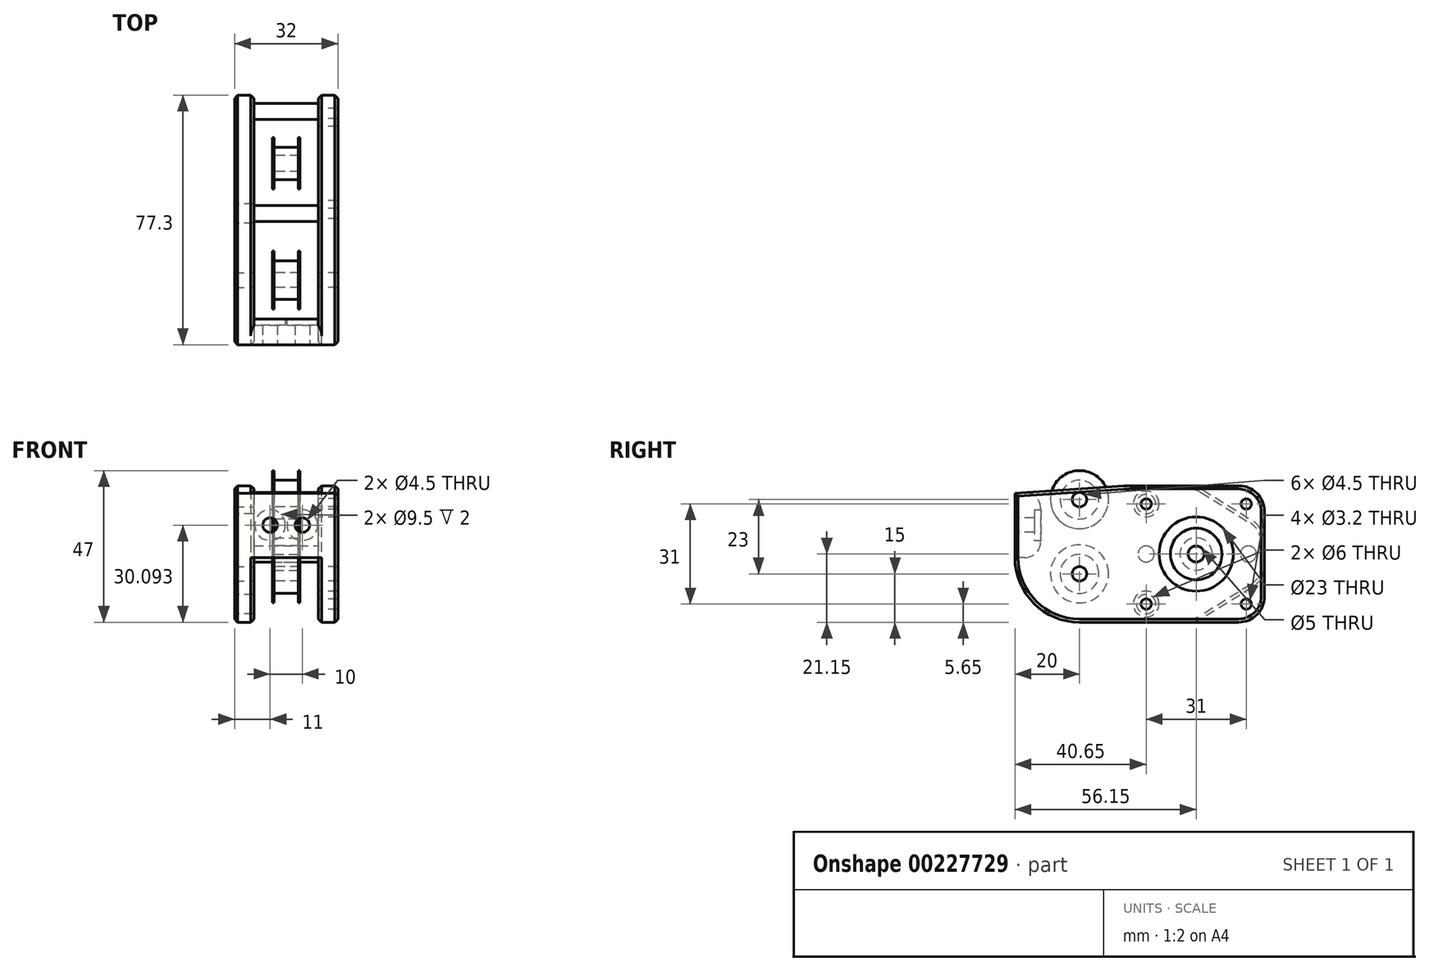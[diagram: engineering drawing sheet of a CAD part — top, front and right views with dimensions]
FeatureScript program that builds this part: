
annotation { "Feature Type Name" : "Feature", "Feature Type Description" : "" }
export const myFeature = defineFeature(function(context is Context, id is Id, definition is map)
    precondition{}
    {
        {
            var Q0;
            Q0=qCreatedBy(makeId("Right.planeOp"),FACE);
            var sketch = newSketch(context, id + "F0", { "sketchPlane" : qUnion([Q0])});
            skLineSegment(sketch, "E0.bottom", {"start": v(0, 0) * mm, "end": v(-20, 0) * mm, "construction": true});
            skLineSegment(sketch, "E0.top", {"start": v(0, 20) * mm, "end": v(-20, 20) * mm, "construction": true});
            skLineSegment(sketch, "E0.left", {"start": v(0, 0) * mm, "end": v(0, 20) * mm, "construction": true});
            skLineSegment(sketch, "E0.right", {"start": v(-20, 0) * mm, "end": v(-20, 20) * mm, "construction": true});
            skCircle(sketch, "E1", {"center": v(20, -5) * mm, "radius": 2.25 * mm});
            skCircle(sketch, "E2", {"center": v(20, -5) * mm, "radius": 9 * mm});
            skCircle(sketch, "E3", {"center": v(20, -5) * mm, "radius": 6 * mm});
            skLineSegment(sketch, "E4", {"start": v(0, 0) * mm, "end": v(0, -20) * mm, "construction": true});
            skLineSegment(sketch, "E5.bottom", {"start": v(77.3, -20) * mm, "end": v(35, -20) * mm, "construction": true});
            skLineSegment(sketch, "E5.top", {"start": v(77.3, 22.3) * mm, "end": v(35, 22.3) * mm, "construction": true});
            skLineSegment(sketch, "E5.left", {"start": v(77.3, -20) * mm, "end": v(77.3, 22.3) * mm, "construction": true});
            skLineSegment(sketch, "E5.right", {"start": v(35, -20) * mm, "end": v(35, 22.3) * mm, "construction": true});
            skLineSegment(sketch, "E6", {"start": v(35, 22.3) * mm, "end": v(77.3, -20) * mm, "construction": true});
            skCircle(sketch, "E7", {"center": v(56.15, 1.15) * mm, "radius": 2.5 * mm});
            skCircle(sketch, "E8", {"center": v(56.15, 1.15) * mm, "radius": 8 * mm});
            skCircle(sketch, "E9", {"center": v(56.15, 1.15) * mm, "radius": 5 * mm});
            skLineSegment(sketch, "E10", {"start": v(35, -20) * mm, "end": v(77.3, 22.3) * mm, "construction": true});
            skCircle(sketch, "E11", {"center": v(40.65, 16.65) * mm, "radius": 1.6 * mm, "construction": true});
            skCircle(sketch, "E12", {"center": v(71.65, 16.65) * mm, "radius": 1.6 * mm, "construction": true});
            skCircle(sketch, "E13", {"center": v(71.65, -14.35) * mm, "radius": 1.6 * mm, "construction": true});
            skCircle(sketch, "E14", {"center": v(40.65, -14.35) * mm, "radius": 1.6 * mm, "construction": true});
            skCircle(sketch, "E15", {"center": v(20, 18) * mm, "radius": 2.25 * mm});
            skCircle(sketch, "E16", {"center": v(20, 18) * mm, "radius": 6 * mm});
            skCircle(sketch, "E17", {"center": v(20, 18) * mm, "radius": 9 * mm});
            skSolve(sketch);
        }
        {
            var Q0;
            Q0=qCreatedBy(makeId("Right.planeOp"),FACE);
            cPlane(context, id + "F1", {"entities" : qUnion([Q0]), "cplaneType" : CPlaneType.OFFSET, "offset" : 10 * mm, "width" : 150 * mm, "height" : 150 * mm});
        }
        {
            var Q0;
            Q0=makeQuery(id+"F0.imprint","IMPRINT",FACE,{"disambiguationData":[TD([[makeQuery(id+"F0.imprint","IMPRINT",EDGE,{"derivedFrom":sQuery(id+"F0.wireOp",EDGE,"E15")}),-1.0]])]});
            var Q1;
            Q1=makeQuery(id+"F0.imprint","IMPRINT",FACE,{"disambiguationData":[TD([[makeQuery(id+"F0.imprint","IMPRINT",EDGE,{"derivedFrom":sQuery(id+"F0.wireOp",EDGE,"E16")}),-1.0]])]});
            extrude(context, id + "F2", {"entities" : qUnion([Q0, Q1]), "endBound" : BoundingType.SYMMETRIC, "depth" : 8.5 * mm});
        }
        {
            var Q0;
            Q0=makeQuery(id+"F0.imprint","IMPRINT",FACE,{"disambiguationData":[TD([[makeQuery(id+"F0.imprint","IMPRINT",EDGE,{"derivedFrom":sQuery(id+"F0.wireOp",EDGE,"E16")}),-1.0]])]});
            extrude(context, id + "F3", {"entities" : qUnion([Q0]), "operationType" : NewBodyOperationType.REMOVE, "endBound" : BoundingType.SYMMETRIC, "depth" : 7.5 * mm});
        }
        {
            var Q0;
            Q0=makeQuery(id+"F0.imprint","IMPRINT",FACE,{"disambiguationData":[TD([[makeQuery(id+"F0.imprint","IMPRINT",EDGE,{"derivedFrom":sQuery(id+"F0.wireOp",EDGE,"E2")}),1.0]])]});
            var Q1;
            Q1=makeQuery(id+"F0.imprint","IMPRINT",FACE,{"disambiguationData":[TD([[makeQuery(id+"F0.imprint","IMPRINT",EDGE,{"derivedFrom":sQuery(id+"F0.wireOp",EDGE,"E1")}),-1.0]])]});
            extrude(context, id + "F4", {"entities" : qUnion([Q0, Q1]), "endBound" : BoundingType.SYMMETRIC, "depth" : 8.5 * mm});
        }
        {
            var Q0;
            Q0=makeQuery(id+"F0.imprint","IMPRINT",FACE,{"disambiguationData":[TD([[makeQuery(id+"F0.imprint","IMPRINT",EDGE,{"derivedFrom":sQuery(id+"F0.wireOp",EDGE,"E2")}),1.0]])]});
            extrude(context, id + "F5", {"entities" : qUnion([Q0]), "operationType" : NewBodyOperationType.REMOVE, "endBound" : BoundingType.SYMMETRIC, "oppositeDirection" : true, "depth" : 7.5 * mm});
        }
        {
            var Q0;
            Q0=makeQuery(id+"F0.imprint","IMPRINT",FACE,{"disambiguationData":[TD([[makeQuery(id+"F0.imprint","IMPRINT",EDGE,{"derivedFrom":sQuery(id+"F0.wireOp",EDGE,"E8")}),1.0]])]});
            var Q1;
            Q1=makeQuery(id+"F0.imprint","IMPRINT",FACE,{"disambiguationData":[TD([[makeQuery(id+"F0.imprint","IMPRINT",EDGE,{"derivedFrom":sQuery(id+"F0.wireOp",EDGE,"E7")}),-1.0]])]});
            extrude(context, id + "F6", {"entities" : qUnion([Q0, Q1]), "endBound" : BoundingType.SYMMETRIC, "depth" : 8.5 * mm});
        }
        {
            var Q0;
            Q0=makeQuery(id+"F0.imprint","IMPRINT",FACE,{"disambiguationData":[TD([[makeQuery(id+"F0.imprint","IMPRINT",EDGE,{"derivedFrom":sQuery(id+"F0.wireOp",EDGE,"E8")}),1.0]])]});
            extrude(context, id + "F7", {"entities" : qUnion([Q0]), "operationType" : NewBodyOperationType.REMOVE, "endBound" : BoundingType.SYMMETRIC, "oppositeDirection" : true, "depth" : 7.5 * mm});
        }
        {
            var Q0;
            Q0=qCreatedBy(id+"F1.planeOp",FACE);
            var sketch = newSketch(context, id + "F8", { "sketchPlane" : qUnion([Q0])});
            skPoint(sketch, "E18.0", {"position": v(0, 20) * mm});
            skPoint(sketch, "E19.0", {"position": v(0, 0) * mm});
            skPoint(sketch, "E20.0", {"position": v(0, -20) * mm});
            skPoint(sketch, "E21.0", {"position": v(77.3, 22.3) * mm});
            skPoint(sketch, "E22.0", {"position": v(20, 18) * mm});
            skPoint(sketch, "E23.0", {"position": v(20, -5) * mm});
            skCircle(sketch, "E24.0", {"center": v(20, -5) * mm, "radius": 2.25 * mm});
            skCircle(sketch, "E25.0", {"center": v(20, 18) * mm, "radius": 2.25 * mm});
            skPoint(sketch, "E26.0", {"position": v(77.3, -20) * mm});
            skCircle(sketch, "E27.0", {"center": v(40.65, 16.65) * mm, "radius": 1.6 * mm});
            skCircle(sketch, "E28.0", {"center": v(40.65, -14.35) * mm, "radius": 1.6 * mm});
            skCircle(sketch, "E29.0", {"center": v(71.65, 16.65) * mm, "radius": 1.6 * mm});
            skCircle(sketch, "E30.0", {"center": v(71.65, -14.35) * mm, "radius": 1.6 * mm});
            skPoint(sketch, "E31.0", {"position": v(56.15, 1.15) * mm});
            skCircle(sketch, "E32", {"center": v(56.15, 1.15) * mm, "radius": 11.5 * mm});
            skPoint(sketch, "E33.0", {"position": v(35, 22.3) * mm});
            skLineSegment(sketch, "E34", {"start": v(0, 20) * mm, "end": v(35, 22.3) * mm});
            skLineSegment(sketch, "E35", {"start": v(35, 22.3) * mm, "end": v(77.3, 22.3) * mm});
            skLineSegment(sketch, "E36", {"start": v(77.3, 22.3) * mm, "end": v(77.3, -20) * mm});
            skLineSegment(sketch, "E37", {"start": v(77.3, -20) * mm, "end": v(0, -20) * mm});
            skLineSegment(sketch, "E38", {"start": v(0, -20) * mm, "end": v(0, 20) * mm});
            skSolve(sketch);
        }
        {
            var Q0;
            Q0=makeQuery(id+"F8.imprint","IMPRINT",FACE,{"disambiguationData":[TD([[makeQuery(id+"F8.imprint","IMPRINT",EDGE,{"derivedFrom":sQuery(id+"F8.wireOp",EDGE,"E24.0")}),-1.0]])]});
            extrude(context, id + "F9", {"entities" : qUnion([Q0]), "depth" : 6 * mm});
        }
        {
            var Q0;
            Q0=makeQuery(id+"F9.opExtrude","SWEPT_EDGE",EDGE,{"disambiguationData":[OSD([sQuery(id+"F8.wireOp",EDGE,"E35"),sQuery(id+"F8.wireOp",EDGE,"E36")])]});
            var Q1;
            Q1=makeQuery(id+"F9.opExtrude","SWEPT_EDGE",EDGE,{"disambiguationData":[OSD([sQuery(id+"F8.wireOp",EDGE,"E36"),sQuery(id+"F8.wireOp",EDGE,"E37")])]});
            fillet(context, id + "F10", {"entities" : qUnion([Q0, Q1]), "radius" : 8 * mm, "tangentPropagation" : true, "allowEdgeOverflow" : false});
        }
        {
            var Q0;
            Q0=makeQuery(id+"F9.opExtrude","SWEPT_EDGE",EDGE,{"disambiguationData":[OSD([sQuery(id+"F8.wireOp",EDGE,"E34"),sQuery(id+"F8.wireOp",EDGE,"E35")])]});
            fillet(context, id + "F11", {"entities" : qUnion([Q0]), "radius" : 40 * mm, "tangentPropagation" : true, "allowEdgeOverflow" : false});
        }
        {
            var Q0;
            Q0=makeQuery(id+"F9.opExtrude","SWEPT_EDGE",EDGE,{"disambiguationData":[OSD([sQuery(id+"F8.wireOp",EDGE,"E37"),sQuery(id+"F8.wireOp",EDGE,"E38")])]});
            fillet(context, id + "F12", {"entities" : qUnion([Q0]), "radius" : 20 * mm, "tangentPropagation" : true, "allowEdgeOverflow" : false});
        }
        {
            var Q0;
            Q0=makeQuery(id+"F9.opExtrude","CAP_FACE",FACE,{"disambiguationData":[OSD([sQuery(id+"F8.wireOp",EDGE,"E24.0"),sQuery(id+"F8.wireOp",EDGE,"E25.0"),sQuery(id+"F8.wireOp",EDGE,"E27.0"),sQuery(id+"F8.wireOp",EDGE,"E28.0"),sQuery(id+"F8.wireOp",EDGE,"E29.0"),sQuery(id+"F8.wireOp",EDGE,"E30.0"),sQuery(id+"F8.wireOp",EDGE,"E32"),sQuery(id+"F8.wireOp",EDGE,"E34"),sQuery(id+"F8.wireOp",EDGE,"E35"),sQuery(id+"F8.wireOp",EDGE,"E36"),sQuery(id+"F8.wireOp",EDGE,"E37"),sQuery(id+"F8.wireOp",EDGE,"E38")])],"isStart":true});
            var sketch = newSketch(context, id + "F13", { "sketchPlane" : qUnion([Q0])});
            skLineSegment(sketch, "E39.0", {"start": v(0, 20) * mm, "end": v(-8, 20.53) * mm});
            skLineSegment(sketch, "E40.0", {"start": v(0, 0) * mm, "end": v(0, 20) * mm});
            skLineSegment(sketch, "E41", {"start": v(-8, 0) * mm, "end": v(-8, 20.53) * mm});
            skPoint(sketch, "E42.orphan", {"position": v(-69.3, -20) * mm});
            skPoint(sketch, "E43.orphan", {"position": v(-33.69, 22.21) * mm});
            skLineSegment(sketch, "E44", {"start": v(-8, 0) * mm, "end": v(0, 0) * mm});
            skSolve(sketch);
        }
        {
            var Q0;
            Q0=makeQuery(id+"F9.opExtrude","SWEPT_BODY",BODY,{"disambiguationData":[OSD([sQuery(id+"F8.wireOp",EDGE,"E24.0"),sQuery(id+"F8.wireOp",EDGE,"E25.0"),sQuery(id+"F8.wireOp",EDGE,"E27.0"),sQuery(id+"F8.wireOp",EDGE,"E28.0"),sQuery(id+"F8.wireOp",EDGE,"E29.0"),sQuery(id+"F8.wireOp",EDGE,"E30.0"),sQuery(id+"F8.wireOp",EDGE,"E32"),sQuery(id+"F8.wireOp",EDGE,"E34"),sQuery(id+"F8.wireOp",EDGE,"E35"),sQuery(id+"F8.wireOp",EDGE,"E36"),sQuery(id+"F8.wireOp",EDGE,"E37"),sQuery(id+"F8.wireOp",EDGE,"E38")])]});
            var Q1;
            Q1=qCreatedBy(makeId("Right.planeOp"),FACE);
            mirror(context, id + "F14", {"entities" : qUnion([Q0]), "mirrorPlane" : qUnion([Q1])});
        }
        {
            var Q0;
            Q0=makeQuery(id+"F13.imprint","IMPRINT",FACE,{"disambiguationData":[TD([[makeQuery(id+"F13.imprint","IMPRINT",EDGE,{"derivedFrom":sQuery(id+"F13.wireOp",EDGE,"E39.0")}),1.0]])]});
            extrude(context, id + "F15", {"entities" : qUnion([Q0]), "endBound" : BoundingType.UP_TO_NEXT, "depth" : 25 * mm});
        }
        {
            var Q0;
            Q0=makeQuery(id+"F9.opExtrude","SWEPT_BODY",BODY,{"disambiguationData":[OSD([sQuery(id+"F8.wireOp",EDGE,"E24.0"),sQuery(id+"F8.wireOp",EDGE,"E25.0"),sQuery(id+"F8.wireOp",EDGE,"E27.0"),sQuery(id+"F8.wireOp",EDGE,"E28.0"),sQuery(id+"F8.wireOp",EDGE,"E29.0"),sQuery(id+"F8.wireOp",EDGE,"E30.0"),sQuery(id+"F8.wireOp",EDGE,"E32"),sQuery(id+"F8.wireOp",EDGE,"E34"),sQuery(id+"F8.wireOp",EDGE,"E35"),sQuery(id+"F8.wireOp",EDGE,"E36"),sQuery(id+"F8.wireOp",EDGE,"E37"),sQuery(id+"F8.wireOp",EDGE,"E38")])]});
            var Q1;
            Q1=makeQuery(id+"F15.opExtrude","SWEPT_BODY",BODY,{"disambiguationData":[OSD([sQuery(id+"F13.wireOp",EDGE,"E39.0"),sQuery(id+"F13.wireOp",EDGE,"E40.0"),sQuery(id+"F13.wireOp",EDGE,"da3027ed-b4a8-42d3-a2ed-4b1a9892917b.0"),sQuery(id+"F13.wireOp",EDGE,"E41")])]});
            var Q2;
            Q2=makeQuery(id+"F14.opPattern","COPY",BODY,{"derivedFrom":makeQuery(id+"F9.opExtrude","SWEPT_BODY",BODY,{"disambiguationData":[OSD([sQuery(id+"F8.wireOp",EDGE,"E24.0"),sQuery(id+"F8.wireOp",EDGE,"E25.0"),sQuery(id+"F8.wireOp",EDGE,"E27.0"),sQuery(id+"F8.wireOp",EDGE,"E28.0"),sQuery(id+"F8.wireOp",EDGE,"E29.0"),sQuery(id+"F8.wireOp",EDGE,"E30.0"),sQuery(id+"F8.wireOp",EDGE,"E32"),sQuery(id+"F8.wireOp",EDGE,"E34"),sQuery(id+"F8.wireOp",EDGE,"E35"),sQuery(id+"F8.wireOp",EDGE,"E36"),sQuery(id+"F8.wireOp",EDGE,"E37"),sQuery(id+"F8.wireOp",EDGE,"E38")])]}),"instanceName":"1"});
            booleanBodies(context, id + "F16", {"operationType" : BooleanOperationType.UNION, "tools" : qUnion([Q0, Q1, Q2])});
        }
        {
            var Q0;
            Q0=makeQuery(id+"F14.opPattern","COPY",FACE,{"derivedFrom":makeQuery(id+"F9.opExtrude","SWEPT_FACE",FACE,{"disambiguationData":[OSD([sQuery(id+"F8.wireOp",EDGE,"E35")])]}),"instanceName":"1"});
            var sketch = newSketch(context, id + "F17", { "sketchPlane" : qUnion([Q0])});
            skLineSegment(sketch, "E45", {"start": v(-16, 80.2) * mm, "end": v(-10, 80.2) * mm});
            skPoint(sketch, "E46.0", {"position": v(-10, 36.31) * mm});
            skPoint(sketch, "E47.0", {"position": v(-16, 36.31) * mm});
            skPoint(sketch, "E48.0", {"position": v(-16, 77.3) * mm});
            skPoint(sketch, "E49.0", {"position": v(-10, 77.3) * mm});
            skLineSegment(sketch, "E50.bottom", {"start": v(-10, 77.3) * mm, "end": v(-16, 77.3) * mm});
            skLineSegment(sketch, "E50.top", {"start": v(-10, 36.31) * mm, "end": v(-16, 36.31) * mm});
            skLineSegment(sketch, "E50.left", {"start": v(-10, 77.3) * mm, "end": v(-10, 36.31) * mm});
            skLineSegment(sketch, "E50.right", {"start": v(-16, 77.3) * mm, "end": v(-16, 36.31) * mm});
            skSolve(sketch);
        }
        {
            var Q0;
            Q0 = qSketchRegion(id + "F17", true);
            extrude(context, id + "F18", {"entities" : qUnion([Q0]), "operationType" : NewBodyOperationType.REMOVE, "endBound" : BoundingType.THROUGH_ALL, "oppositeDirection" : true, "depth" : 25 * mm});
        }
        {
            var Q0;
            Q0=makeQuery(id+"F14.opPattern","COPY",FACE,{"derivedFrom":makeQuery(id+"F9.opExtrude","CAP_FACE",FACE,{"disambiguationData":[OSD([sQuery(id+"F8.wireOp",EDGE,"E24.0"),sQuery(id+"F8.wireOp",EDGE,"E25.0"),sQuery(id+"F8.wireOp",EDGE,"E27.0"),sQuery(id+"F8.wireOp",EDGE,"E28.0"),sQuery(id+"F8.wireOp",EDGE,"E29.0"),sQuery(id+"F8.wireOp",EDGE,"E30.0"),sQuery(id+"F8.wireOp",EDGE,"E32"),sQuery(id+"F8.wireOp",EDGE,"E34"),sQuery(id+"F8.wireOp",EDGE,"E35"),sQuery(id+"F8.wireOp",EDGE,"E36"),sQuery(id+"F8.wireOp",EDGE,"E37"),sQuery(id+"F8.wireOp",EDGE,"E38")])],"isStart":false}),"instanceName":"1"});
            var sketch = newSketch(context, id + "F19", { "sketchPlane" : qUnion([Q0])});
            skPoint(sketch, "E51.0", {"position": v(-56.15, 1.15) * mm});
            skPoint(sketch, "E52.0", {"position": v(-77.3, 1.15) * mm});
            skLineSegment(sketch, "E53", {"start": v(-36.31, 22.3) * mm, "end": v(-56.15, 22.3) * mm});
            skLineSegment(sketch, "E54", {"start": v(-56.15, 22.3) * mm, "end": v(-77.3, 9.15) * mm});
            skLineSegment(sketch, "E55", {"start": v(-77.3, 9.15) * mm, "end": v(-77.3, 1.15) * mm});
            skLineSegment(sketch, "E56", {"start": v(-77.3, 1.15) * mm, "end": v(-77.3, -6.85) * mm});
            skLineSegment(sketch, "E57", {"start": v(-77.3, -6.85) * mm, "end": v(-56.15, -20) * mm});
            skLineSegment(sketch, "E58", {"start": v(-56.15, -20) * mm, "end": v(-36.31, -20) * mm});
            skLineSegment(sketch, "E59", {"start": v(-36.31, -20) * mm, "end": v(-36.31, 22.3) * mm});
            skCircle(sketch, "E60.0", {"center": v(-40.65, 16.65) * mm, "radius": 1.6 * mm, "construction": true});
            skCircle(sketch, "E61.0", {"center": v(-40.65, -14.35) * mm, "radius": 1.6 * mm, "construction": true});
            skCircle(sketch, "E62", {"center": v(-40.65, -14.35) * mm, "radius": 3 * mm});
            skCircle(sketch, "E63", {"center": v(-40.65, 16.65) * mm, "radius": 3 * mm});
            skSolve(sketch);
        }
        {
            var Q0;
            Q0 = qSketchRegion(id + "F19", true);
            var Q1;
            Q1=makeQuery(id+"F14.opPattern","COPY",FACE,{"derivedFrom":makeQuery(id+"F9.opExtrude","CAP_FACE",FACE,{"disambiguationData":[OSD([sQuery(id+"F8.wireOp",EDGE,"E24.0"),sQuery(id+"F8.wireOp",EDGE,"E25.0"),sQuery(id+"F8.wireOp",EDGE,"E27.0"),sQuery(id+"F8.wireOp",EDGE,"E28.0"),sQuery(id+"F8.wireOp",EDGE,"E29.0"),sQuery(id+"F8.wireOp",EDGE,"E30.0"),sQuery(id+"F8.wireOp",EDGE,"E32"),sQuery(id+"F8.wireOp",EDGE,"E34"),sQuery(id+"F8.wireOp",EDGE,"E35"),sQuery(id+"F8.wireOp",EDGE,"E36"),sQuery(id+"F8.wireOp",EDGE,"E37"),sQuery(id+"F8.wireOp",EDGE,"E38")])],"isStart":true}),"instanceName":"1"});
            extrude(context, id + "F20", {"entities" : qUnion([Q0]), "operationType" : NewBodyOperationType.ADD, "endBound" : BoundingType.UP_TO_SURFACE, "oppositeDirection" : true, "endBoundEntityFace" : qUnion([Q1]), "depth" : 25 * mm});
        }
        {
            var Q0;
            Q0=makeQuery(id+"F20.opExtrude","SWEPT_EDGE",EDGE,{"disambiguationData":[OSD([sQuery(id+"F19.wireOp",EDGE,"E54"),sQuery(id+"F19.wireOp",EDGE,"E55")])]});
            var Q1;
            Q1=makeQuery(id+"F20.opExtrude","SWEPT_EDGE",EDGE,{"disambiguationData":[OSD([sQuery(id+"F19.wireOp",EDGE,"E56"),sQuery(id+"F19.wireOp",EDGE,"E57")])]});
            var Q2;
            Q2=makeQuery(id+"F20.opExtrude","SWEPT_EDGE",EDGE,{"disambiguationData":[OSD([sQuery(id+"F19.wireOp",EDGE,"E53"),sQuery(id+"F19.wireOp",EDGE,"E54")])]});
            var Q3;
            Q3=makeQuery(id+"F20.opExtrude","SWEPT_EDGE",EDGE,{"disambiguationData":[OSD([sQuery(id+"F19.wireOp",EDGE,"E57"),sQuery(id+"F19.wireOp",EDGE,"E58")])]});
            fillet(context, id + "F21", {"entities" : qUnion([Q0, Q1, Q2, Q3]), "radius" : 8 * mm, "tangentPropagation" : true, "allowEdgeOverflow" : false});
        }
        {
            var Q0;
            Q0=makeQuery(id+"F15.opExtrude","SWEPT_EDGE",EDGE,{"disambiguationData":[OSD([sQuery(id+"F8.wireOp",EDGE,"E34"),sQuery(id+"F13.wireOp",EDGE,"E39.0"),sQuery(id+"F13.wireOp",EDGE,"E41")])]});
            var Q1;
            Q1=makeQuery(id+"F15.opExtrude","SWEPT_EDGE",EDGE,{"disambiguationData":[OSD([sQuery(id+"F13.wireOp",EDGE,"E41"),sQuery(id+"F13.wireOp",EDGE,"E44")])]});
            fillet(context, id + "F22", {"entities" : qUnion([Q0, Q1]), "radius" : 5 * mm, "tangentPropagation" : true, "allowEdgeOverflow" : false});
        }
        {
            var Q0;
            Q0=makeQuery(id+"F14.opPattern","COPY",EDGE,{"derivedFrom":makeQuery(id+"F9.opExtrude","CAP_EDGE",EDGE,{"disambiguationData":[OSD([sQuery(id+"F8.wireOp",EDGE,"E34")])],"isStart":false}),"instanceName":"1"});
            var Q1;
            Q1=makeQuery(id+"F14.opPattern","COPY",EDGE,{"derivedFrom":makeQuery(id+"F9.opExtrude","CAP_EDGE",EDGE,{"disambiguationData":[OSD([sQuery(id+"F8.wireOp",EDGE,"E34")])],"isStart":true}),"instanceName":"1"});
            var Q2;
            Q2=makeQuery(id+"F9.opExtrude","CAP_EDGE",EDGE,{"disambiguationData":[OSD([sQuery(id+"F8.wireOp",EDGE,"E34")])],"isStart":true});
            var Q3;
            Q3=makeQuery(id+"F9.opExtrude","CAP_EDGE",EDGE,{"disambiguationData":[OSD([sQuery(id+"F8.wireOp",EDGE,"E34")])],"isStart":false});
            chamfer(context, id + "F23", {"entities" : qUnion([Q0, Q1, Q2, Q3]), "width" : 1 * mm, "tangentPropagation" : true});
        }
        {
            var Q0;
            Q0=makeQuery(id+"F9.opExtrude","CAP_FACE",FACE,{"disambiguationData":[OSD([sQuery(id+"F8.wireOp",EDGE,"E24.0"),sQuery(id+"F8.wireOp",EDGE,"E25.0"),sQuery(id+"F8.wireOp",EDGE,"E27.0"),sQuery(id+"F8.wireOp",EDGE,"E28.0"),sQuery(id+"F8.wireOp",EDGE,"E29.0"),sQuery(id+"F8.wireOp",EDGE,"E30.0"),sQuery(id+"F8.wireOp",EDGE,"E32"),sQuery(id+"F8.wireOp",EDGE,"E34"),sQuery(id+"F8.wireOp",EDGE,"E35"),sQuery(id+"F8.wireOp",EDGE,"E36"),sQuery(id+"F8.wireOp",EDGE,"E37"),sQuery(id+"F8.wireOp",EDGE,"E38")])],"isStart":true});
            var sketch = newSketch(context, id + "F24", { "sketchPlane" : qUnion([Q0])});
            skPoint(sketch, "E64.0", {"position": v(-76.3, 1.15) * mm});
            skCircle(sketch, "E65", {"center": v(-72.3, 1.15) * mm, "radius": 2.5 * mm});
            skCircle(sketch, "E66.0", {"center": v(-40.65, 16.65) * mm, "radius": 1.6 * mm, "construction": true});
            skCircle(sketch, "E67", {"center": v(-40.65, 1.15) * mm, "radius": 2.5 * mm});
            skSolve(sketch);
        }
        {
            var Q0;
            Q0 = qSketchRegion(id + "F24", true);
            extrude(context, id + "F25", {"entities" : qUnion([Q0]), "operationType" : NewBodyOperationType.ADD, "endBound" : BoundingType.UP_TO_NEXT, "depth" : 25 * mm});
        }
        {
            var Q0;
            {var subQ0=makeQuery(id+"F9.opExtrude","SWEPT_FACE",FACE,{"disambiguationData":[OSD([sQuery(id+"F8.wireOp",EDGE,"E38")])]});Q0=makeQuery(id+"F16.opBoolean","MERGE",FACE,{"derivedFrom":[subQ0,makeQuery(id+"F14.opPattern","COPY",FACE,{"derivedFrom":subQ0,"instanceName":"1"}),makeQuery(id+"F15.opExtrude","SWEPT_FACE",FACE,{"disambiguationData":[OSD([sQuery(id+"F13.wireOp",EDGE,"E40.0")])]})]});}
            var sketch = newSketch(context, id + "F26", { "sketchPlane" : qUnion([Q0])});
            skLineSegment(sketch, "E68.0", {"start": v(-10, 5) * mm, "end": v(-10, 15.19) * mm, "construction": true});
            skLineSegment(sketch, "E69.0", {"start": v(10, 5) * mm, "end": v(10, 15.19) * mm, "construction": true});
            skLineSegment(sketch, "E70", {"start": v(-10, 10.1) * mm, "end": v(0, 10.1) * mm, "construction": true});
            skLineSegment(sketch, "E71", {"start": v(0, 10.1) * mm, "end": v(10, 10.1) * mm, "construction": true});
            skCircle(sketch, "E72", {"center": v(-5, 10.1) * mm, "radius": 2.25 * mm});
            skCircle(sketch, "E73", {"center": v(5, 10.1) * mm, "radius": 2.25 * mm});
            skSolve(sketch);
        }
        {
            var Q0;
            Q0 = qSketchRegion(id + "F26", true);
            extrude(context, id + "F27", {"entities" : qUnion([Q0]), "operationType" : NewBodyOperationType.REMOVE, "endBound" : BoundingType.UP_TO_NEXT, "oppositeDirection" : true, "depth" : 25 * mm});
        }
        {
            var Q0;
            Q0=makeQuery(id+"F15.opExtrude","SWEPT_FACE",FACE,{"disambiguationData":[OSD([sQuery(id+"F13.wireOp",EDGE,"E41")])]});
            var sketch = newSketch(context, id + "F28", { "sketchPlane" : qUnion([Q0])});
            skCircle(sketch, "E74.0", {"center": v(5, 10.1) * mm, "radius": 2.25 * mm, "construction": true});
            skCircle(sketch, "E75.0", {"center": v(-5, 10.1) * mm, "radius": 2.25 * mm, "construction": true});
            skCircle(sketch, "E76", {"center": v(5, 10.1) * mm, "radius": 4.75 * mm});
            skCircle(sketch, "E77", {"center": v(-5, 10.1) * mm, "radius": 4.75 * mm});
            skSolve(sketch);
        }
        {
            var Q0;
            Q0 = qSketchRegion(id + "F28", true);
            extrude(context, id + "F29", {"entities" : qUnion([Q0]), "operationType" : NewBodyOperationType.REMOVE, "oppositeDirection" : true, "depth" : 2 * mm});
        }
        {
            var Q0;
            Q0=makeQuery(id+"F20.opExtrude","CAP_EDGE",EDGE,{"disambiguationData":[OSD([sQuery(id+"F19.wireOp",EDGE,"E63")])],"isStart":true});
            var Q1;
            Q1=makeQuery(id+"F20.opExtrude","CAP_EDGE",EDGE,{"disambiguationData":[OSD([sQuery(id+"F19.wireOp",EDGE,"E62")])],"isStart":true});
            chamfer(context, id + "F30", {"entities" : qUnion([Q0, Q1]), "width" : 1 * mm, "tangentPropagation" : true});
        }
    });
